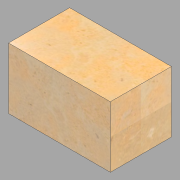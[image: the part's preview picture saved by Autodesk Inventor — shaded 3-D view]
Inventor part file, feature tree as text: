
AUTODESK INVENTOR PART (.ipt)
format: ipt  version: 2022.2 (Build 262287000, 287)  size: 131,072 bytes
history: native  units: in
note: dims shown in document units (in); Inventor stores cm internally (conversion verified against a paired STEP export)
features: extrude x1, sketch x1
ambient origin geometry x8: Origin, YZ Plane, XZ Plane, XY Plane, X Axis, Y Axis, Z Axis, Center Point
bodies: Solid1 (feature_tree)
feature tree (2):
  extrude  "Extrusion1"  Depth=3.0in
  sketch  "Sketch1"  dims[d0=3.0in d1=3.0in d2=5.0in d3=0.0in]
